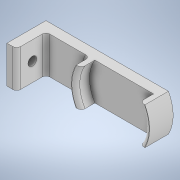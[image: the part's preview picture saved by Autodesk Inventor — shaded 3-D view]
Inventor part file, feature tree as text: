
AUTODESK INVENTOR PART (.ipt)
format: ipt  version: 2020 (Build 240168000, 168)  size: 184,832 bytes
history: native  units: in
note: dims shown in document units (in); Inventor stores cm internally (conversion verified against a paired STEP export)
features: sketch x7, extrude x6, fillet x5, projected_geometry x1
ambient origin geometry x8: Origin, YZ Plane, XZ Plane, XY Plane, X Axis, Y Axis, Z Axis, Center Point
bodies: Solid1 (feature_tree)
feature tree (19):
  extrude  "Extrusion1"  Depth=1.5748in
  extrude  "Extrusion2"  Depth=0.1969in TaperAngle=0.0deg
  extrude  "Extrusion3"  Depth=0.374in
  extrude  "Extrusion4"  TaperAngle=90.0deg  [1 undecoded]
  extrude  "Extrusion5"  Depth=0.1969in TaperAngle=0.0deg
  sketch  "Sketch6"  dims[d14=0.1969in d15=0.5906in d16=0.0in d17=0.1772in d18=0.5906in d19=0.0in d20=0.0787in d21=0.0787in d22=0.0787in]
  extrude  "Extrusion6"  Depth=0.0787in TaperAngle=0.0deg
  fillet  "Fillet1"  Radius=0.1772in
  fillet  "Fillet2"  Radius=0.5906in
  fillet  "Fillet3"  Radius=0.0787in
  fillet  "Fillet4"  Radius=0.0787in
  fillet  "Fillet6"  Radius=0.0787in
  sketch  "Sketch1"  dims[d0=1.3976in d1=1.5748in]
  sketch  "Sketch2"  dims[d2=0.2756in d3=0.0in d4=0.1969in d5=0.0in]
  sketch  "Sketch3"  dims[d6=0.748in d7=0.374in]
  sketch  "Sketch4"  dims[d8=0.0in d9=0.0in d10=90.0deg]
  projected_geometry  "Projected Loop1"
  sketch  "Sketch5"  dims[d11=1.7717in d12=0.1969in d13=0.0in]
  sketch  "Sketch7"  dims[d23=0.0787in d25=0.0787in]
note: 1 required parameter value undecoded (feature->parameter linkage not recoverable at this tier; creation-order binding heuristic only, values carry confidence <= 0.55)
